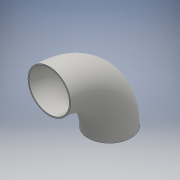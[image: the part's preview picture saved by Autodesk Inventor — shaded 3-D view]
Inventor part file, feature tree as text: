
AUTODESK INVENTOR PART (.ipt)
format: ipt  version: 2016 (Build 200138000, 138)  size: 152,064 bytes
history: native  units: in
note: dims shown in document units (in); Inventor stores cm internally (conversion verified against a paired STEP export)
features: other x3, sketch x2
ambient origin geometry x8: Origin, YZ Plane, XZ Plane, XY Plane, X Axis, Y Axis, Z Axis, Center Point
bodies: Solid1 (feature_tree)
feature tree (5):
  other  "joelho 90 12 inch ANSI B16.9.ipt"
  other  "Solid2::joelho 90 12 inch ANSI B16.9.ipt"
  other  "TaggingFeature1"
  sketch  "Sketch2"  dims[d0=0.3937in]
  sketch  "Sketch3"
